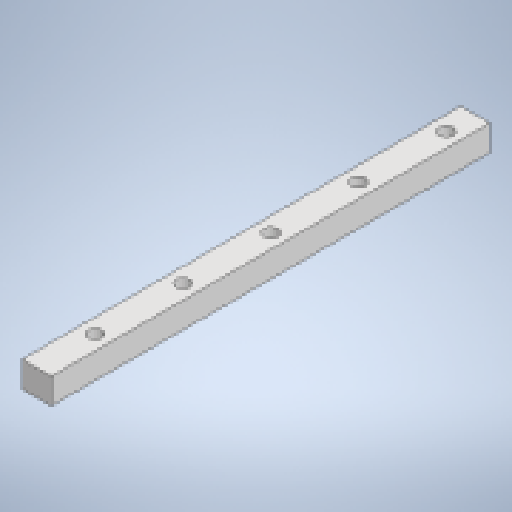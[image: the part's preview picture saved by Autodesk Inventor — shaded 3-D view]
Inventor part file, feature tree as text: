
AUTODESK INVENTOR PART (.ipt)
format: ipt  version: 2023 (Build 270158000, 158)  size: 161,792 bytes
history: native  units: mm
features: extrude x3, sketch x3, pattern_linear x1
ambient origin geometry x8: Origin, YZ Plane, XZ Plane, XY Plane, X Axis, Y Axis, Z Axis, Center Point
bodies: Solid1 (feature_tree)
feature tree (7):
  extrude  "Extrusion1"  Depth=17.5mm
  extrude  "Extrusion2"  Depth=300.0mm
  extrude  "Extrusion3"  Depth=8.5mm TaperAngle=0.0deg
  pattern_linear  "Rectangular Pattern1"  Spacing1=9.5mm  [1 undecoded]
  sketch  "Sketch1"  dims[d0=20.0mm d1=17.5mm]
  sketch  "Sketch2"  dims[d2=300.0mm d3=0.0mm d4=6.0mm]
  sketch  "Sketch3"  dims[d5=20.0mm d6=800.0mm d7=0.0mm d8=9.5mm d9=8.5mm d10=0.0mm d11=180.0mm d13=60.0mm]
note: 1 required parameter value undecoded (feature->parameter linkage not recoverable at this tier; creation-order binding heuristic only, values carry confidence <= 0.55)
